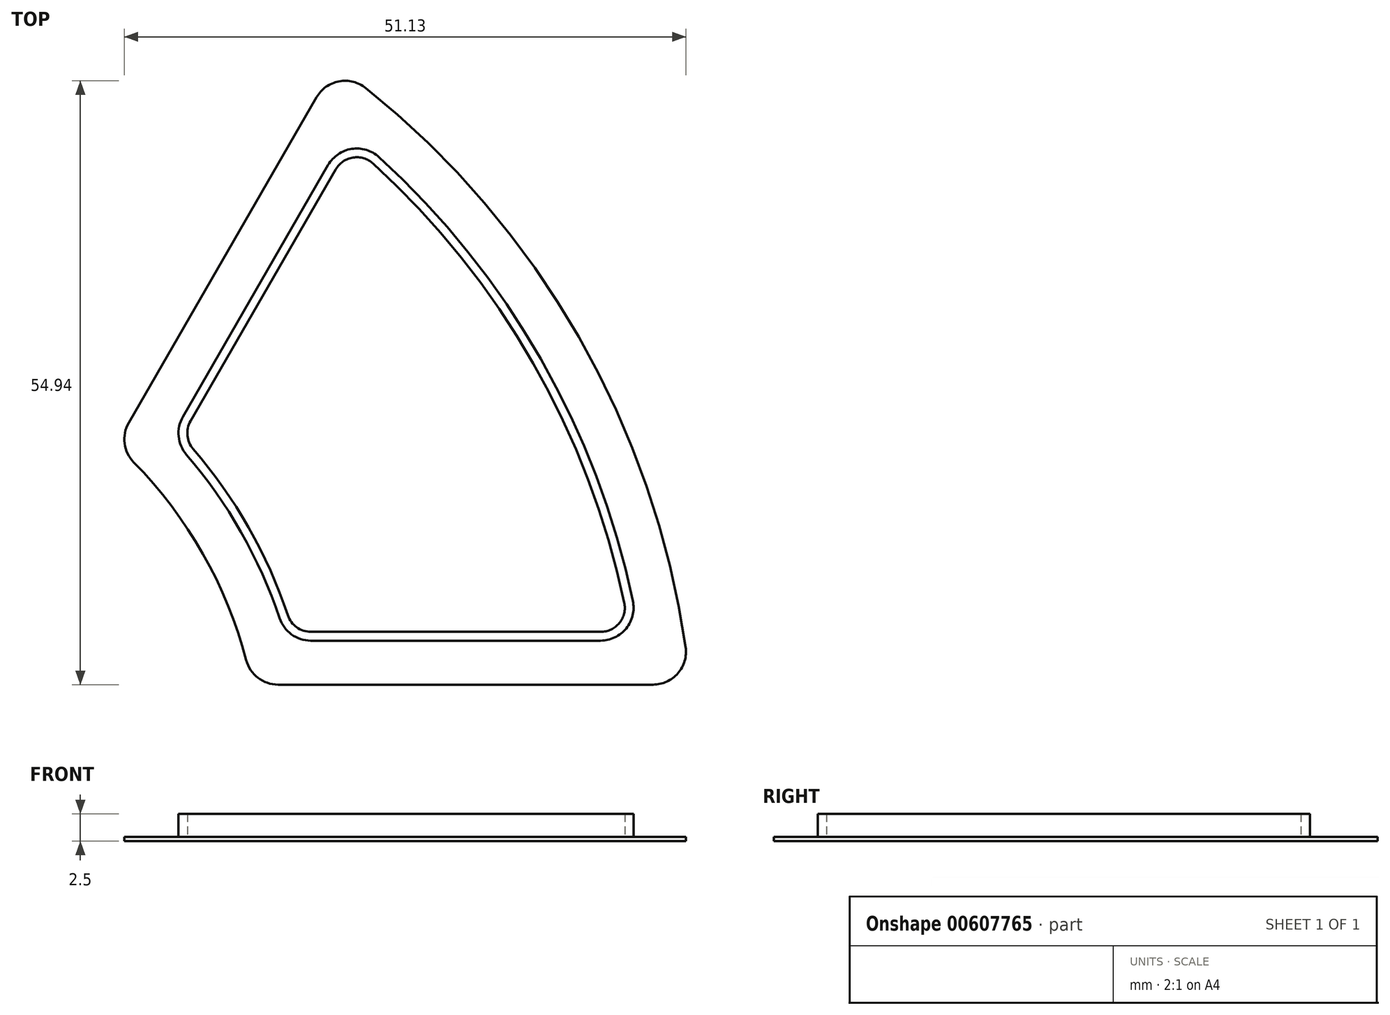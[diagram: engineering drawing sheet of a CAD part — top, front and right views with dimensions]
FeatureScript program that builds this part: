
annotation { "Feature Type Name" : "Feature", "Feature Type Description" : "" }
export const myFeature = defineFeature(function(context is Context, id is Id, definition is map)
    precondition{}
    {
        {
            var Q0;
            Q0=qCreatedBy(makeId("Top.planeOp"),FACE);
            var sketch = newSketch(context, id + "F0", { "sketchPlane" : qUnion([Q0])});
            skArc(sketch, "E0", {"start": v(74.12, 15.62) * mm, "mid": v(65.74, 37.63) * mm, "end": v(51.01, 56) * mm});
            skArc(sketch, "E1", {"start": v(41.96, 14.05) * mm, "mid": v(38.45, 21.9) * mm, "end": v(33.5, 28.92) * mm});
            skLineSegment(sketch, "E2", {"start": v(44.8, 12) * mm, "end": v(71.19, 12) * mm});
            skLineSegment(sketch, "E3", {"start": v(33.17, 32.38) * mm, "end": v(46.4, 55.28) * mm});
            skArc(sketch, "E4.0", {"start": v(78.93, 11.43) * mm, "mid": v(69.2, 39.63) * mm, "end": v(49.8, 62.29) * mm});
            skLineSegment(sketch, "E4.1", {"start": v(41.83, 8) * mm, "end": v(75.96, 8) * mm});
            skArc(sketch, "E4.2", {"start": v(38.93, 10.24) * mm, "mid": v(34.99, 19.9) * mm, "end": v(28.7, 28.23) * mm});
            skLineSegment(sketch, "E4.3", {"start": v(28.23, 31.83) * mm, "end": v(45.33, 61.44) * mm});
            skPoint(sketch, "E5.visualSharp", {"position": v(48.21, 58.43) * mm});
            skArc(sketch, "E5.filletArc", {"start": v(51.01, 56) * mm, "mid": v(48.53, 56.75) * mm, "end": v(46.4, 55.28) * mm});
            skPoint(sketch, "E6.visualSharp", {"position": v(32.08, 30.48) * mm});
            skArc(sketch, "E6.filletArc", {"start": v(33.17, 32.38) * mm, "mid": v(32.78, 30.6) * mm, "end": v(33.5, 28.92) * mm});
            skPoint(sketch, "E7.visualSharp", {"position": v(42.6, 12) * mm});
            skArc(sketch, "E7.filletArc", {"start": v(41.96, 14.05) * mm, "mid": v(43.05, 12.57) * mm, "end": v(44.8, 12) * mm});
            skPoint(sketch, "E8.visualSharp", {"position": v(74.8, 12) * mm});
            skArc(sketch, "E8.filletArc", {"start": v(71.19, 12) * mm, "mid": v(73.52, 13.1) * mm, "end": v(74.12, 15.62) * mm});
            skPoint(sketch, "E9.visualSharp", {"position": v(47.04, 64.4) * mm});
            skArc(sketch, "E9.filletArc", {"start": v(49.8, 62.29) * mm, "mid": v(47.37, 62.9) * mm, "end": v(45.33, 61.44) * mm});
            skPoint(sketch, "E10.visualSharp", {"position": v(27.06, 29.8) * mm});
            skArc(sketch, "E10.filletArc", {"start": v(28.23, 31.83) * mm, "mid": v(27.86, 29.95) * mm, "end": v(28.7, 28.23) * mm});
            skPoint(sketch, "E11.visualSharp", {"position": v(39.45, 8) * mm});
            skArc(sketch, "E11.filletArc", {"start": v(38.93, 10.24) * mm, "mid": v(40, 8.62) * mm, "end": v(41.83, 8) * mm});
            skPoint(sketch, "E12.visualSharp", {"position": v(79.35, 8) * mm});
            skArc(sketch, "E12.filletArc", {"start": v(75.96, 8) * mm, "mid": v(78.23, 9.04) * mm, "end": v(78.93, 11.43) * mm});
            skArc(sketch, "E13.0", {"start": v(33.86, 31.98) * mm, "mid": v(33.58, 30.67) * mm, "end": v(34.1, 29.44) * mm});
            skArc(sketch, "E13.1", {"start": v(42.72, 14.3) * mm, "mid": v(39.15, 22.3) * mm, "end": v(34.1, 29.44) * mm});
            skLineSegment(sketch, "E13.2", {"start": v(33.86, 31.98) * mm, "end": v(47.09, 54.88) * mm});
            skArc(sketch, "E13.3", {"start": v(42.72, 14.3) * mm, "mid": v(43.52, 13.21) * mm, "end": v(44.8, 12.8) * mm});
            skArc(sketch, "E13.4", {"start": v(50.47, 55.4) * mm, "mid": v(48.65, 55.96) * mm, "end": v(47.09, 54.88) * mm});
            skArc(sketch, "E13.5", {"start": v(73.34, 15.45) * mm, "mid": v(65.05, 37.23) * mm, "end": v(50.47, 55.4) * mm});
            skArc(sketch, "E13.6", {"start": v(71.19, 12.8) * mm, "mid": v(72.9, 13.61) * mm, "end": v(73.34, 15.45) * mm});
            skLineSegment(sketch, "E13.7", {"start": v(44.8, 12.8) * mm, "end": v(71.19, 12.8) * mm});
            skSolve(sketch);
        }
        {
            var Q0;
            Q0=makeQuery(id+"F0.imprint","IMPRINT",FACE,{"disambiguationData":[TD([[makeQuery(id+"F0.imprint","IMPRINT",EDGE,{"derivedFrom":sQuery(id+"F0.wireOp",EDGE,"E0")}),1.0]])]});
            extrude(context, id + "F1", {"entities" : qUnion([Q0]), "depth" : 2.5 * mm, "offsetDistance" : 25 * mm});
        }
        {
            var Q0;
            Q0=makeQuery(id+"F0.imprint","IMPRINT",FACE,{"disambiguationData":[TD([[makeQuery(id+"F0.imprint","IMPRINT",EDGE,{"derivedFrom":sQuery(id+"F0.wireOp",EDGE,"E0")}),-1.0]])]});
            var Q1;
            Q1=makeQuery(id+"F0.imprint","IMPRINT",FACE,{"disambiguationData":[TD([[makeQuery(id+"F0.imprint","IMPRINT",EDGE,{"derivedFrom":sQuery(id+"F0.wireOp",EDGE,"E13.0")}),1.0]])]});
            extrude(context, id + "F2", {"entities" : qUnion([Q0, Q1]), "operationType" : NewBodyOperationType.ADD, "depth" : 0.4 * mm, "offsetDistance" : 25 * mm});
        }
    });
